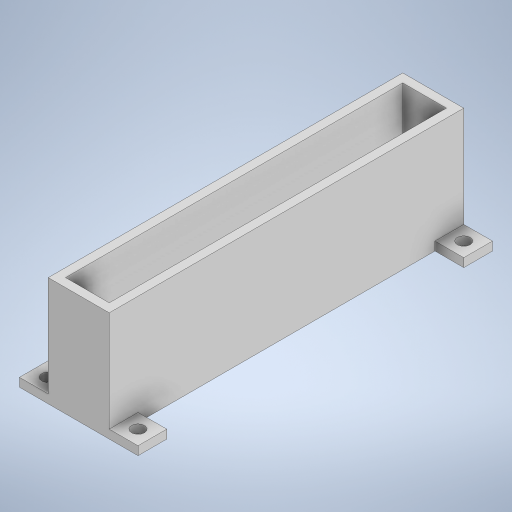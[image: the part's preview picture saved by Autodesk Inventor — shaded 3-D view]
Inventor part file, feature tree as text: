
AUTODESK INVENTOR PART (.ipt)
format: ipt  version: 2024 (Build 280153000, 153)  size: 252,928 bytes
history: native  units: mm
features: extrude x2, sketch x2
ambient origin geometry x8: Origin, YZ Plane, XZ Plane, XY Plane, X Axis, Y Axis, Z Axis, Center Point
bodies: Solid1 (feature_tree)
feature tree (4):
  extrude  "Extrusion1"  Depth=117.2mm
  extrude  "Extrusion2"  Depth=35.0mm TaperAngle=0.0deg
  sketch  "Sketch1"  dims[d0=15.2mm d1=117.2mm]
  sketch  "Sketch2"  dims[d2=3.0mm d3=35.0mm d4=0.0mm d5=4.5mm d6=5.0mm d7=5.0mm d8=5.0mm d9=5.0mm d10=3.0mm d11=0.0mm]
